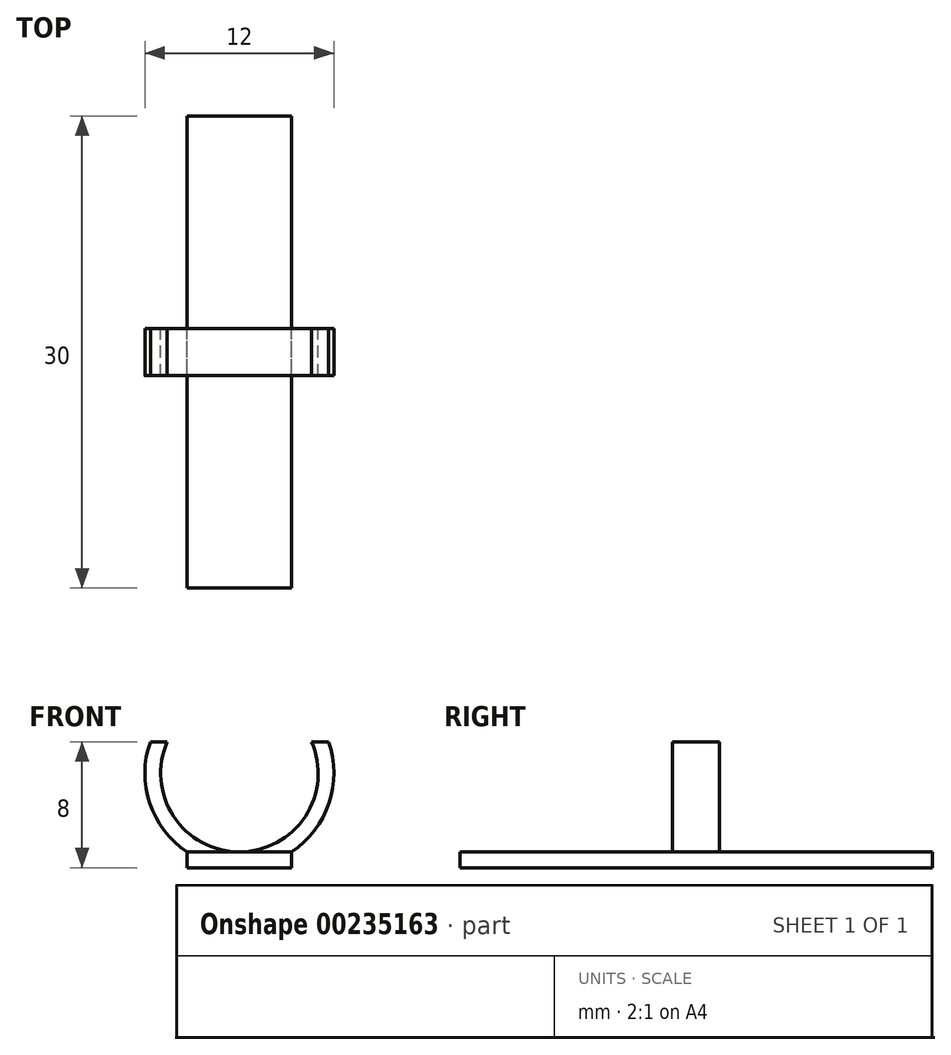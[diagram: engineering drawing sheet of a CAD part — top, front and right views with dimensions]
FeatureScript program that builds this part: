
annotation { "Feature Type Name" : "Feature", "Feature Type Description" : "" }
export const myFeature = defineFeature(function(context is Context, id is Id, definition is map)
    precondition{}
    {
        {
            var Q0;
            Q0=qCreatedBy(makeId("Front.planeOp"),FACE);
            var sketch = newSketch(context, id + "F0", { "sketchPlane" : qUnion([Q0])});
            skLineSegment(sketch, "E0.bottom", {"start": v(-3.32, 1) * mm, "end": v(3.32, 1) * mm});
            skLineSegment(sketch, "E0.top", {"start": v(-3.32, 0) * mm, "end": v(3.32, 0) * mm});
            skLineSegment(sketch, "E0.left", {"start": v(-3.32, 1) * mm, "end": v(-3.32, 0) * mm});
            skLineSegment(sketch, "E0.right", {"start": v(3.32, 1) * mm, "end": v(3.32, 0) * mm});
            skArc(sketch, "E1", {"start": v(-4.58, 8) * mm, "mid": v(0, 1) * mm, "end": v(4.58, 8) * mm});
            skArc(sketch, "E2.0", {"start": v(-5.66, 8) * mm, "mid": v(0, 0) * mm, "end": v(5.66, 8) * mm});
            skLineSegment(sketch, "E3", {"start": v(-5.66, 8) * mm, "end": v(-4.58, 8) * mm});
            skLineSegment(sketch, "E4.trimOffspring", {"start": v(4.58, 8) * mm, "end": v(5.66, 8) * mm});
            skSolve(sketch);
        }
        {
            var Q0;
            {var subQ0=sQuery(id+"F0.wireOp",EDGE,"E0.right");Q0=makeQuery(id+"F0.imprint","IMPRINT",FACE,{"disambiguationData":[TD([[makeQuery(id+"F0.imprint","IMPRINT",EDGE,{"derivedFrom":subQ0}),-1.0]])]});}
            var Q1;
            {var subQ0=sQuery(id+"F0.wireOp",EDGE,"E0.left");Q1=makeQuery(id+"F0.imprint","IMPRINT",FACE,{"disambiguationData":[TD([[makeQuery(id+"F0.imprint","IMPRINT",EDGE,{"derivedFrom":subQ0}),1.0]])]});}
            var Q2;
            {var subQ0=sQuery(id+"F0.wireOp",EDGE,"E2.0");var subQ1=sQuery(id+"F0.wireOp",EDGE,"E0.bottom");var subQ2=makeQuery(id+"F0.imprint","INTERSECT",VERTEX,{"disambiguationData":[OD(0.0)],"derivedFrom":[subQ1,subQ0]});Q2=makeQuery(id+"F0.imprint","IMPRINT",FACE,{"disambiguationData":[TD([[makeQuery(id+"F0.imprint","IMPRINT",EDGE,{"disambiguationData":[TD([[subQ2,-1.0]])],"derivedFrom":subQ1}),-1.0]])]});}
            extrude(context, id + "F1", {"entities" : qUnion([Q0, Q1, Q2]), "endBound" : BoundingType.SYMMETRIC, "depth" : 30 * mm});
        }
        {
            var Q0;
            {var subQ5=sQuery(id+"F0.wireOp",EDGE,"E3");Q0=makeQuery(id+"F0.imprint","IMPRINT",FACE,{"disambiguationData":[TD([[makeQuery(id+"F0.imprint","IMPRINT",EDGE,{"derivedFrom":subQ5}),-1.0]])]});}
            var Q1;
            {var subQ5=sQuery(id+"F0.wireOp",EDGE,"E4.trimOffspring");Q1=makeQuery(id+"F0.imprint","IMPRINT",FACE,{"disambiguationData":[TD([[makeQuery(id+"F0.imprint","IMPRINT",EDGE,{"derivedFrom":subQ5}),-1.0]])]});}
            extrude(context, id + "F2", {"entities" : qUnion([Q0, Q1]), "operationType" : NewBodyOperationType.ADD, "endBound" : BoundingType.SYMMETRIC, "depth" : 3 * mm});
        }
    });
